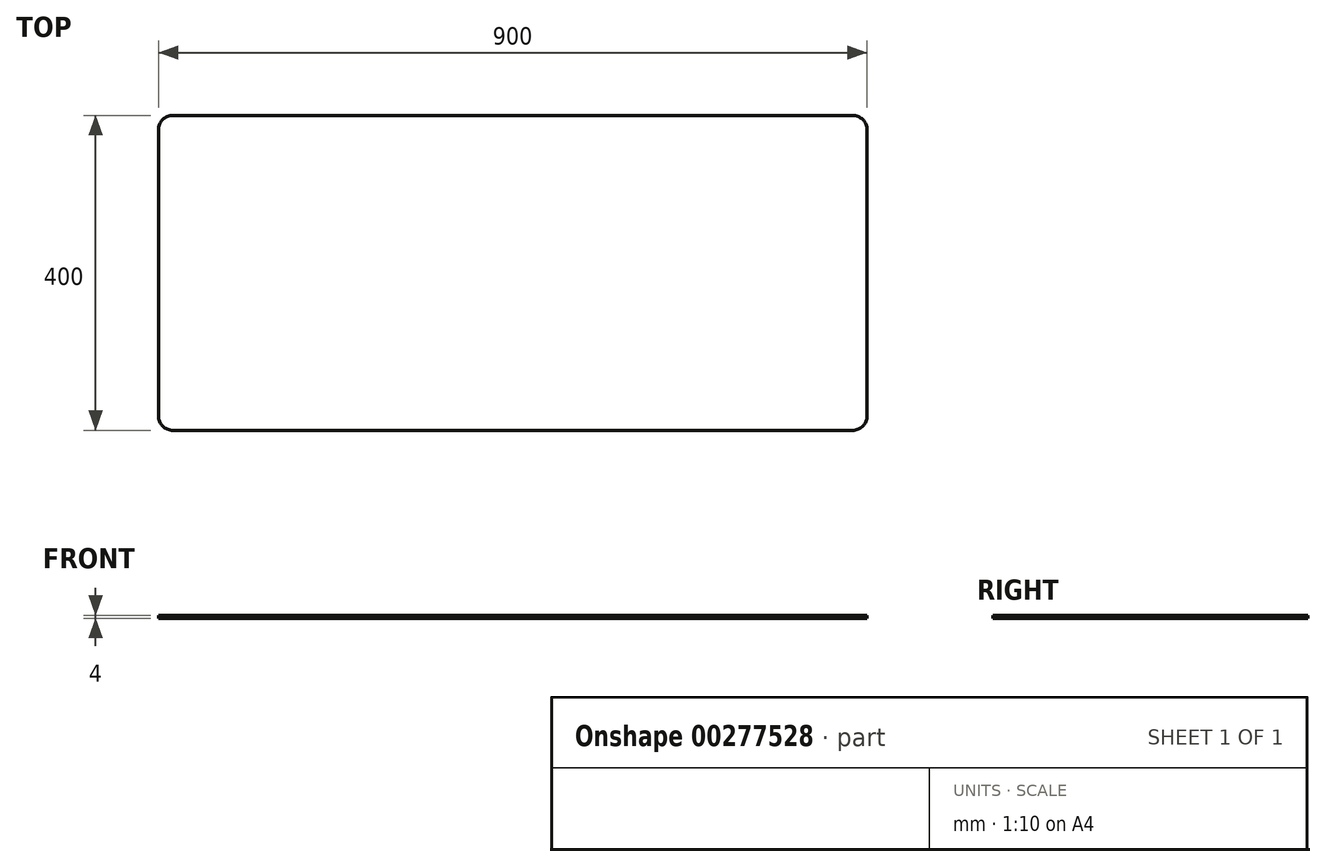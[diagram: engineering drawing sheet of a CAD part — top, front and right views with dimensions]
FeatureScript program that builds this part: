
annotation { "Feature Type Name" : "Feature", "Feature Type Description" : "" }
export const myFeature = defineFeature(function(context is Context, id is Id, definition is map)
    precondition{}
    {
        {
            var Q0;
            Q0=qCreatedBy(makeId("Top.planeOp"),FACE);
            var sketch = newSketch(context, id + "F0", { "sketchPlane" : qUnion([Q0])});
            skLineSegment(sketch, "E0.bottom", {"start": v(-431.74, 200) * mm, "end": v(431.74, 200) * mm});
            skLineSegment(sketch, "E0.top", {"start": v(-431.74, -200) * mm, "end": v(431.74, -200) * mm});
            skLineSegment(sketch, "E0.left", {"start": v(-450, 181.74) * mm, "end": v(-450, -181.74) * mm});
            skLineSegment(sketch, "E0.right", {"start": v(450, 181.74) * mm, "end": v(450, -181.74) * mm});
            skPoint(sketch, "E0.middle", {"position": v(0, 0) * mm});
            skPoint(sketch, "E1.visualSharp", {"position": v(-450, 200) * mm});
            skArc(sketch, "E1.filletArc", {"start": v(-431.74, 200) * mm, "mid": v(-444.65, 194.65) * mm, "end": v(-450, 181.74) * mm});
            skPoint(sketch, "E2.visualSharp", {"position": v(450, 200) * mm});
            skArc(sketch, "E2.filletArc", {"start": v(450, 181.74) * mm, "mid": v(444.65, 194.65) * mm, "end": v(431.74, 200) * mm});
            skPoint(sketch, "E3.visualSharp", {"position": v(450, -200) * mm});
            skArc(sketch, "E3.filletArc", {"start": v(431.74, -200) * mm, "mid": v(444.65, -194.65) * mm, "end": v(450, -181.74) * mm});
            skPoint(sketch, "E4.visualSharp", {"position": v(-450, -200) * mm});
            skArc(sketch, "E4.filletArc", {"start": v(-450, -181.74) * mm, "mid": v(-444.65, -194.65) * mm, "end": v(-431.74, -200) * mm});
            skSolve(sketch);
        }
        {
            var Q0;
            Q0=makeQuery(id+"F0.imprint","IMPRINT",FACE,{"disambiguationData":[TD([[makeQuery(id+"F0.imprint","IMPRINT",EDGE,{"derivedFrom":sQuery(id+"F0.wireOp",EDGE,"E0.bottom")}),-1.0]])]});
            extrude(context, id + "F1", {"entities" : qUnion([Q0]), "depth" : 4 * mm});
        }
    });
